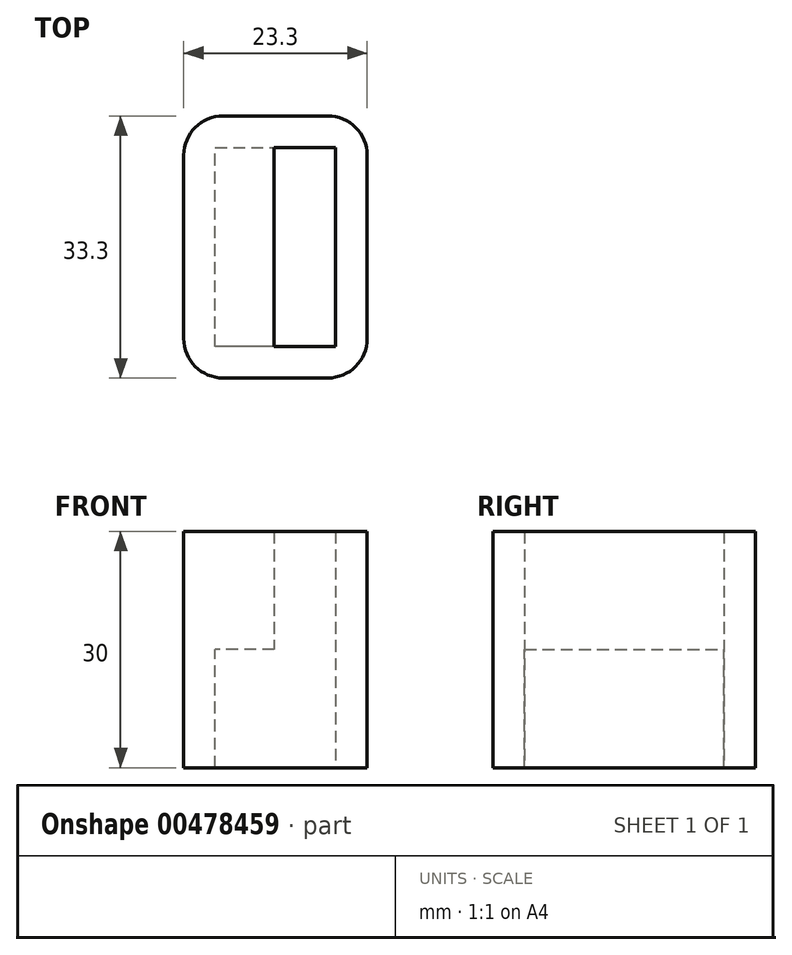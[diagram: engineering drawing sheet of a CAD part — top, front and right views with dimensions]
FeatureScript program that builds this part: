
annotation { "Feature Type Name" : "Feature", "Feature Type Description" : "" }
export const myFeature = defineFeature(function(context is Context, id is Id, definition is map)
    precondition{}
    {
        {
            var Q0;
            Q0=qCreatedBy(makeId("Top.planeOp"),FACE);
            var sketch = newSketch(context, id + "F0", { "sketchPlane" : qUnion([Q0])});
            skLineSegment(sketch, "E0.bottom", {"start": v(-3.9, -12.65) * mm, "end": v(3.9, -12.65) * mm});
            skLineSegment(sketch, "E0.top", {"start": v(-3.9, 12.65) * mm, "end": v(3.9, 12.65) * mm});
            skLineSegment(sketch, "E0.left", {"start": v(-3.9, -12.65) * mm, "end": v(-3.9, 12.65) * mm});
            skLineSegment(sketch, "E0.right", {"start": v(3.9, -12.65) * mm, "end": v(3.9, 12.65) * mm});
            skPoint(sketch, "E0.middle", {"position": v(0, 0) * mm});
            skLineSegment(sketch, "E1.bottom", {"start": v(-7.9, -16.65) * mm, "end": v(7.9, -16.65) * mm});
            skLineSegment(sketch, "E1.top", {"start": v(-7.9, 16.65) * mm, "end": v(7.9, 16.65) * mm});
            skLineSegment(sketch, "E1.left", {"start": v(-7.9, -16.65) * mm, "end": v(-7.9, 16.65) * mm});
            skLineSegment(sketch, "E1.right", {"start": v(7.9, -16.65) * mm, "end": v(7.9, 16.65) * mm});
            skSolve(sketch);
        }
        {
            var Q0;
            Q0=makeQuery(id+"F0.imprint","IMPRINT",FACE,{"disambiguationData":[TD([[makeQuery(id+"F0.imprint","IMPRINT",EDGE,{"derivedFrom":sQuery(id+"F0.wireOp",EDGE,"E0.bottom")}),-1.0]])]});
            extrude(context, id + "F1", {"entities" : qUnion([Q0]), "depth" : 15 * mm});
        }
        {
            var Q0;
            Q0=qCreatedBy(makeId("Top.planeOp"),FACE);
            var sketch = newSketch(context, id + "F2", { "sketchPlane" : qUnion([Q0])});
            skLineSegment(sketch, "E2.bottom", {"start": v(3.9, -12.65) * mm, "end": v(-11.4, -12.65) * mm});
            skLineSegment(sketch, "E2.top", {"start": v(-11.4, 12.65) * mm, "end": v(3.9, 12.65) * mm});
            skLineSegment(sketch, "E2.left", {"start": v(-11.4, -12.65) * mm, "end": v(-11.4, 12.65) * mm});
            skLineSegment(sketch, "E2.right", {"start": v(3.9, -12.65) * mm, "end": v(3.9, 12.65) * mm});
            skPoint(sketch, "E3", {"position": v(7.9, 0) * mm});
            skLineSegment(sketch, "E4.bottom", {"start": v(5.9, -16.65) * mm, "end": v(-15.4, -16.65) * mm});
            skLineSegment(sketch, "E4.top", {"start": v(5.9, 16.65) * mm, "end": v(-15.4, 16.65) * mm});
            skLineSegment(sketch, "E4.left", {"start": v(5.9, -16.65) * mm, "end": v(5.9, 16.65) * mm});
            skLineSegment(sketch, "E4.right", {"start": v(-15.4, -16.65) * mm, "end": v(-15.4, 16.65) * mm});
            skPoint(sketch, "E5", {"position": v(5.9, 0) * mm});
            skLineSegment(sketch, "E6", {"start": v(-7.9, 16.65) * mm, "end": v(-7.9, -16.65) * mm});
            skSolve(sketch);
        }
        {
            var Q0;
            Q0=makeQuery(id+"F2.imprint","IMPRINT",FACE,{"disambiguationData":[TD([[makeQuery(id+"F2.imprint","IMPRINT",EDGE,{"derivedFrom":sQuery(id+"F2.wireOp",EDGE,"E2.bottom")}),1.0]])]});
            extrude(context, id + "F3", {"entities" : qUnion([Q0]), "operationType" : NewBodyOperationType.ADD, "oppositeDirection" : true, "depth" : 15 * mm});
        }
        {
            var Q0;
            {var subQ0=sQuery(id+"F0.wireOp",EDGE,"E1.right");var subQ1=sQuery(id+"F0.wireOp",EDGE,"E1.top");var subQ2=sQuery(id+"F0.wireOp",EDGE,"E1.bottom");Q0=makeQuery(id+"F3.boolean.opBoolean","SPLIT",FACE,{"disambiguationData":[TD([makeQuery(id+"F1.opExtrude","SWEPT_FACE",FACE,{"disambiguationData":[OSD([subQ2])]})])],"derivedFrom":makeQuery(id+"F1.opExtrude","CAP_FACE",FACE,{"disambiguationData":[OSD([sQuery(id+"F0.wireOp",EDGE,"E0.bottom"),sQuery(id+"F0.wireOp",EDGE,"E0.top"),sQuery(id+"F0.wireOp",EDGE,"E0.left"),sQuery(id+"F0.wireOp",EDGE,"E0.right"),subQ2,subQ1,sQuery(id+"F0.wireOp",EDGE,"E1.left"),subQ0])],"isStart":true})});}
            var Q1;
            Q1=makeQuery(id+"F3.opExtrude","CAP_FACE",FACE,{"disambiguationData":[OSD([sQuery(id+"F2.wireOp",EDGE,"E2.bottom"),sQuery(id+"F2.wireOp",EDGE,"E2.top"),sQuery(id+"F2.wireOp",EDGE,"E2.left"),sQuery(id+"F2.wireOp",EDGE,"E2.right"),sQuery(id+"F2.wireOp",EDGE,"E4.bottom"),sQuery(id+"F2.wireOp",EDGE,"E4.top"),sQuery(id+"F2.wireOp",EDGE,"E4.left"),sQuery(id+"F2.wireOp",EDGE,"E4.right")])],"isStart":false});
            extrude(context, id + "F4", {"entities" : qUnion([Q0]), "operationType" : NewBodyOperationType.ADD, "endBound" : BoundingType.UP_TO_SURFACE, "endBoundEntityFace" : qUnion([Q1]), "depth" : 25 * mm});
        }
        {
            var Q0;
            {var subQ0=sQuery(id+"F2.wireOp",EDGE,"E2.left");Q0=makeQuery(id+"F2.imprint","IMPRINT",FACE,{"disambiguationData":[TD([[makeQuery(id+"F2.imprint","IMPRINT",EDGE,{"derivedFrom":subQ0}),1.0]])]});}
            var Q1;
            {var subQ0=sQuery(id+"F2.wireOp",EDGE,"E2.left");Q1=makeQuery(id+"F2.imprint","IMPRINT",FACE,{"disambiguationData":[TD([[makeQuery(id+"F2.imprint","IMPRINT",EDGE,{"derivedFrom":subQ0}),-1.0]])]});}
            var Q2;
            Q2=makeQuery(id+"F1.opExtrude","CAP_FACE",FACE,{"disambiguationData":[OSD([sQuery(id+"F0.wireOp",EDGE,"E0.bottom"),sQuery(id+"F0.wireOp",EDGE,"E0.top"),sQuery(id+"F0.wireOp",EDGE,"E0.left"),sQuery(id+"F0.wireOp",EDGE,"E0.right"),sQuery(id+"F0.wireOp",EDGE,"E1.bottom"),sQuery(id+"F0.wireOp",EDGE,"E1.top"),sQuery(id+"F0.wireOp",EDGE,"E1.left"),sQuery(id+"F0.wireOp",EDGE,"E1.right")])],"isStart":false});
            extrude(context, id + "F5", {"entities" : qUnion([Q0, Q1]), "operationType" : NewBodyOperationType.ADD, "endBound" : BoundingType.UP_TO_SURFACE, "endBoundEntityFace" : qUnion([Q2]), "depth" : 25 * mm});
        }
        {
            var Q0;
            {var subQ0=sQuery(id+"F2.wireOp",EDGE,"E4.right");var subQ1=sQuery(id+"F2.wireOp",EDGE,"E4.bottom");Q0=makeQuery(id+"F5.boolean.opBoolean","MERGE",EDGE,{"derivedFrom":[makeQuery(id+"F3.opExtrude","SWEPT_EDGE",EDGE,{"disambiguationData":[OSD([subQ1,subQ0])]}),makeQuery(id+"F5.opExtrude","SWEPT_EDGE",EDGE,{"disambiguationData":[OSD([subQ1,subQ0])]})]});}
            var Q1;
            {var subQ0=sQuery(id+"F2.wireOp",EDGE,"E4.right");var subQ1=sQuery(id+"F2.wireOp",EDGE,"E4.top");Q1=makeQuery(id+"F5.boolean.opBoolean","MERGE",EDGE,{"derivedFrom":[makeQuery(id+"F3.opExtrude","SWEPT_EDGE",EDGE,{"disambiguationData":[OSD([subQ1,subQ0])]}),makeQuery(id+"F5.opExtrude","SWEPT_EDGE",EDGE,{"disambiguationData":[OSD([subQ1,subQ0])]})]});}
            var Q2;
            {var subQ0=sQuery(id+"F0.wireOp",EDGE,"E1.right");var subQ1=sQuery(id+"F0.wireOp",EDGE,"E1.top");Q2=makeQuery(id+"F4.boolean.opBoolean","MERGE",EDGE,{"derivedFrom":[makeQuery(id+"F1.opExtrude","SWEPT_EDGE",EDGE,{"disambiguationData":[OSD([subQ1,subQ0])]}),makeQuery(id+"F4.opExtrude","SWEPT_EDGE",EDGE,{"disambiguationData":[OSD([subQ1,subQ0])]})]});}
            var Q3;
            {var subQ0=sQuery(id+"F0.wireOp",EDGE,"E1.right");var subQ1=sQuery(id+"F0.wireOp",EDGE,"E1.bottom");Q3=makeQuery(id+"F4.boolean.opBoolean","MERGE",EDGE,{"derivedFrom":[makeQuery(id+"F1.opExtrude","SWEPT_EDGE",EDGE,{"disambiguationData":[OSD([subQ1,subQ0])]}),makeQuery(id+"F4.opExtrude","SWEPT_EDGE",EDGE,{"disambiguationData":[OSD([subQ1,subQ0])]})]});}
            fillet(context, id + "F6", {"entities" : qUnion([Q0, Q1, Q2, Q3]), "radius" : 5 * mm, "tangentPropagation" : true, "allowEdgeOverflow" : false});
        }
    });
